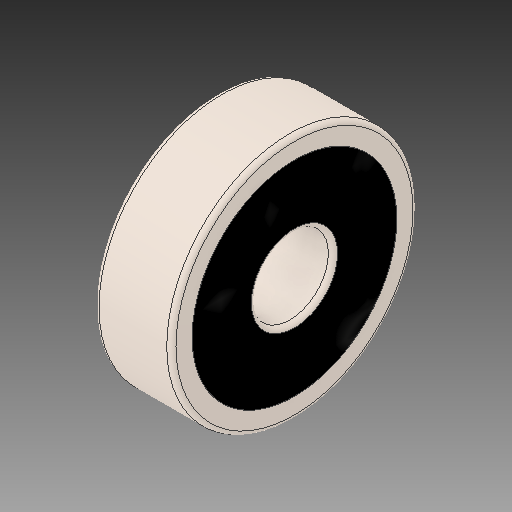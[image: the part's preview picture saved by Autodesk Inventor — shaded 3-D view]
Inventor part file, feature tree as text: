
AUTODESK INVENTOR PART (.ipt)
format: ipt  version: 2018 (Build 220112000, 112)  size: 2,296,320 bytes
history: imported  units: mm
features: other x22, sketch x2, imported_body x1
ambient origin geometry x8: Origin, YZ Plane, XZ Plane, XY Plane, X Axis, Y Axis, Z Axis, Center Point
bodies: Solid1 (imported_parasolid), Solid2 (imported_parasolid), Solid3 (imported_parasolid), Solid4 (imported_parasolid), Solid5 (imported_parasolid), Solid6 (imported_parasolid), Solid7 (imported_parasolid), Solid8 (imported_parasolid), Solid9 (imported_parasolid), Solid10 (imported_parasolid), Solid11 (imported_parasolid), Solid12 (imported_parasolid), Solid13 (imported_parasolid), Solid14 (imported_parasolid), Solid15 (imported_parasolid), Solid16 (imported_parasolid), Solid17 (imported_parasolid), Solid18 (imported_parasolid), Solid19 (imported_parasolid), Solid20 (imported_parasolid)
feature tree (25):
  other  "SKF 625_CPY.ipt"
  other  "Solid1::SKF 625_CPY.ipt"
  other  "Solid2::SKF 625_CPY.ipt"
  other  "Solid3::SKF 625_CPY.ipt"
  other  "Solid4::SKF 625_CPY.ipt"
  other  "Solid5::SKF 625_CPY.ipt"
  other  "Solid6::SKF 625_CPY.ipt"
  other  "Solid7::SKF 625_CPY.ipt"
  other  "Solid8::SKF 625_CPY.ipt"
  other  "Solid9::SKF 625_CPY.ipt"
  other  "Solid10::SKF 625_CPY.ipt"
  other  "Solid11::SKF 625_CPY.ipt"
  other  "Solid12::SKF 625_CPY.ipt"
  other  "Solid13::SKF 625_CPY.ipt"
  other  "Solid14::SKF 625_CPY.ipt"
  other  "Solid15::SKF 625_CPY.ipt"
  other  "Solid16::SKF 625_CPY.ipt"
  other  "Solid17::SKF 625_CPY.ipt"
  other  "Solid18::SKF 625_CPY.ipt"
  other  "Solid19::SKF 625_CPY.ipt"
  other  "Solid20::SKF 625_CPY.ipt"
  other  "TaggingFeature1"
  sketch  "Sketch1"  dims[d0=10.0mm]
  sketch  "Sketch2"
  imported_body  NMx_Import_Brep_tag  [imported B-rep: ~49 faces, bbox_mm=None]
